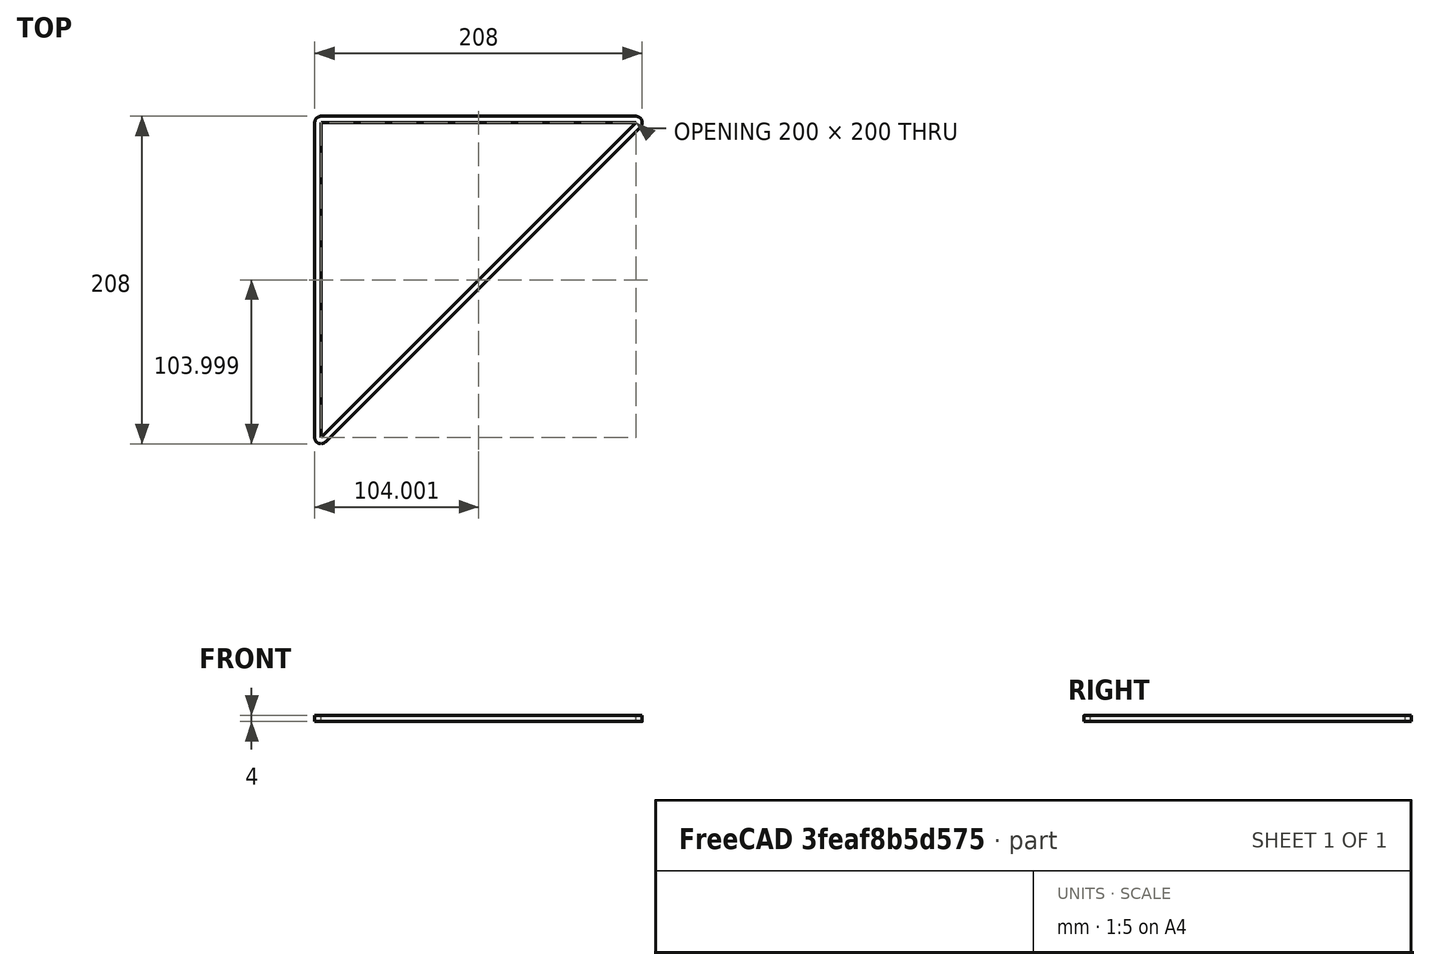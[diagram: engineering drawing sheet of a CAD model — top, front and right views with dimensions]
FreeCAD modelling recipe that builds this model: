
FCSTD DOCUMENT  (FreeCAD 0.19R24366 (Git))
Label: LongLines
License: All rights reserved
LicenseURL: http://en.wikipedia.org/wiki/All_rights_reserved
objects: Sketcher::SketchObject×1, PartDesign::Pad×1, PartDesign::Body×1
note: 4 computed .brp shape members not serialized (recipe doc carries the construction recipe); baked Part::Feature solids carry a one-line shape summary decoded from their .brp

FEATURE [Sketcher::SketchObject] Sketch
  FullyConstrained = true
  MapMode = 5
  Support = -> [XY_Plane]
  sketch-geometry (13):
    g0: LineSegment StartX=-58.5786 StartY=58.5786 StartZ=0 EndX=-58.5786 EndY=-141.421 EndZ=0
    g1: LineSegment StartX=-62.5786 StartY=-141.421 StartZ=0 EndX=-62.5786 EndY=58.5786 EndZ=0
    g2: LineSegment StartX=-58.5786 StartY=58.5786 StartZ=0 EndX=141.421 EndY=58.5786 EndZ=0
    g3: LineSegment StartX=141.421 StartY=62.5786 StartZ=0 EndX=-58.5786 EndY=62.5786 EndZ=0
    g4: LineSegment StartX=-58.5786 StartY=-141.421 StartZ=0 EndX=141.421 EndY=58.5786 EndZ=0
    g5: LineSegment StartX=-58.5786 StartY=58.5786 StartZ=0 EndX=-62.5786 EndY=58.5786 EndZ=0
    g6: LineSegment StartX=-58.5786 StartY=58.5786 StartZ=0 EndX=-58.5786 EndY=62.5786 EndZ=0
    g7: LineSegment StartX=-55.7502 StartY=-144.25 StartZ=0 EndX=144.25 EndY=55.7502 EndZ=0
    g8: LineSegment StartX=141.421 StartY=58.5786 StartZ=0 EndX=144.25 EndY=55.7502 EndZ=0
    g9: ArcOfCircle CenterX=-58.5786 CenterY=58.5786 CenterZ=0 NormalX=0 NormalY=0 NormalZ=1 AngleXU=0 Radius=4 StartAngle=1.5708 EndAngle=3.14159
    g10: ArcOfCircle CenterX=141.421 CenterY=58.5786 CenterZ=0 NormalX=0 NormalY=0 NormalZ=1 AngleXU=0 Radius=4 StartAngle=5.49779 EndAngle=7.85398
    g11: ArcOfCircle CenterX=-58.5786 CenterY=-141.421 CenterZ=0 NormalX=0 NormalY=0 NormalZ=1 AngleXU=0 Radius=4 StartAngle=3.14159 EndAngle=5.49779
    g12: Circle CenterX=0 CenterY=0 CenterZ=0 NormalX=0 NormalY=0 NormalZ=1 AngleXU=0 Radius=58.5786
  constraints (33):
    c: Vertical(g0)
    c: Vertical(g1)
    c: Coincident(g0,g2)
    c: Horizontal(g2)
    c: Horizontal(g3)
    c: Equal(g2,g0)
    c: Coincident(g4,g0)
    c: Coincident(g4,g2)
    c: Coincident(g5,g0)
    c: PointOnObject(g5,g1)
    c: Horizontal(g5)
    c: Coincident(g6,g0)
    c: Vertical(g6)
    c: DistanceX(g5,g6) = 4
    c: Coincident(g8,g2)
    c: PointOnObject(g8,g7)
    c: Perpendicular(g7,g8)
    c: Parallel(g4,g7)
    c: Coincident(g9,g0)
    c: Coincident(g9,g1)
    c: Coincident(g9,g3)
    c: Coincident(g3,g6)
    c: Tangent(g3,g10) = -1.5708
    c: Tangent(g7,g10) = -1.5708
    c: Tangent(g1,g11) = 1.5708
    c: Tangent(g7,g11) = -1.5708
    c: Tangent(g12,g2)
    c: Tangent(g12,g0)
    c: Tangent(g12,g4)
    c: Coincident(g0,g11)
    c: Coincident(g2,g10)
    c: DistanceY(g1,g1) = 200
    c: Coincident(g12,g-1)
FEATURE [PartDesign::Pad] Pad
  Direction = (1,1,1)
  Length = 4
  Length2 = 100
  Profile = -> Sketch
  Type = 0
FEATURE [PartDesign::Body] Body
  Group = -> [Sketch,Pad]
  Origin = -> Origin
  Tip = -> Pad
